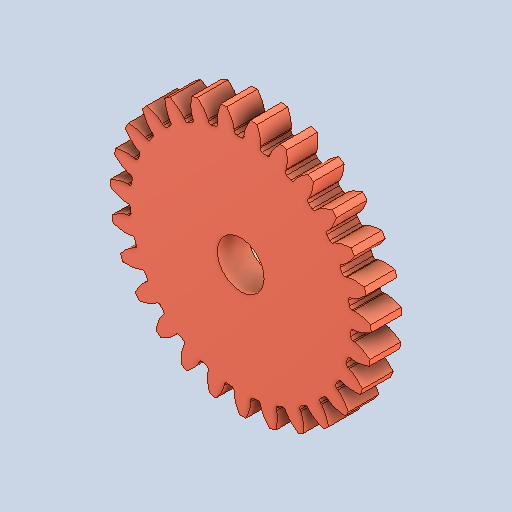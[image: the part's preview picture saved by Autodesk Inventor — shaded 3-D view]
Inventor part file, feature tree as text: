
AUTODESK INVENTOR PART (.ipt)
format: ipt  version: 2022 (Build 260153000, 153)  size: 458,752 bytes
history: imported  units: in
note: dims shown in document units (in); Inventor stores cm internally (conversion verified against a paired STEP export)
features: imported_body x1
ambient origin geometry x8: Origin, YZ Plane, XZ Plane, XY Plane, X Axis, Y Axis, Z Axis, Center Point
bodies: Solid1 (imported_parasolid), Body2 (imported_parasolid)
feature tree (1):
  imported_body  NMx_Import_Brep_tag  [imported B-rep: ~17 faces, bbox_mm=[18.405008, 11.321499, 4.1656]]
